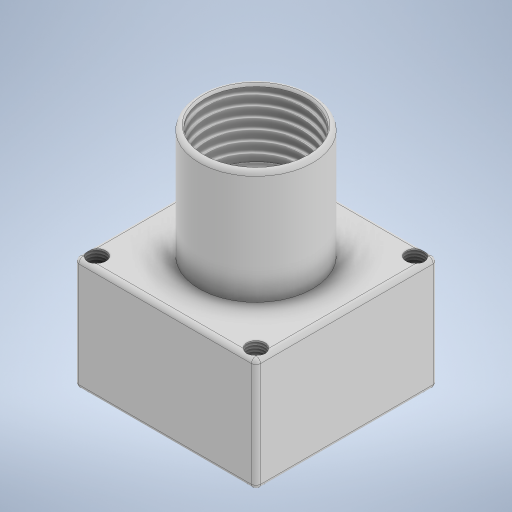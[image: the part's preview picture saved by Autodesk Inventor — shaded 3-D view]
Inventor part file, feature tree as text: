
AUTODESK INVENTOR PART (.ipt)
format: ipt  version: 2024 (Build 280153000, 153)  size: 348,672 bytes
history: native  units: mm
features: extrude x6, sketch x6, thread x4, other x1, fillet x1
ambient origin geometry x8: Origin, YZ Plane, XZ Plane, XY Plane, X Axis, Y Axis, Z Axis, Center Point
bodies: Body1 (feature_tree)
feature tree (18):
  other  "Sólido1"
  extrude  "Extrusión1"  Depth=80.0mm
  extrude  "Extrusión2"  Depth=50.0mm
  extrude  "Extrusión3"  Depth=50.0mm TaperAngle=0.0deg
  extrude  "Extrusión4"  Depth=30.0mm TaperAngle=0.0deg
  extrude  "Extrusión5"  Depth=70.0mm
  extrude  "Extrusión6"  Depth=2.0mm
  thread  "Rosca1"  [1 undecoded]
  thread  "Rosca2"  [1 undecoded]
  thread  "Rosca3"  [1 undecoded]
  thread  "Rosca4"  [1 undecoded]
  fillet  "Empalme1"  Radius=70.0mm
  sketch  "Boceto1"  dims[d0=80.0mm d1=80.0mm]
  sketch  "Boceto2"  dims[d2=50.0mm d3=0.0mm d4=50.0mm]
  sketch  "Boceto3"  dims[d5=45.0mm d6=50.0mm d7=0.0mm]
  sketch  "Boceto4"  dims[d8=45.0mm d9=30.0mm d10=0.0mm]
  sketch  "Boceto5"  dims[d11=70.0mm d12=70.0mm]
  sketch  "Boceto6"  dims[d13=8.0mm d14=8.0mm d15=8.0mm d16=8.0mm d17=50.0mm d18=0.0mm d19=70.0mm d20=70.0mm d22=8.0mm d23=8.0mm d24=50.0mm d25=0.0mm d26=70.0mm d27=70.0mm d28=8.0mm d29=8.0mm d30=50.0mm d31=0.0mm d32=30.0mm d33=0.0mm d34=50.0mm d35=0.0mm d36=50.0mm d37=0.0mm d38=50.0mm d39=0.0mm d40=2.0mm]
note: 4 required parameter values undecoded (feature->parameter linkage not recoverable at this tier; creation-order binding heuristic only, values carry confidence <= 0.55)
